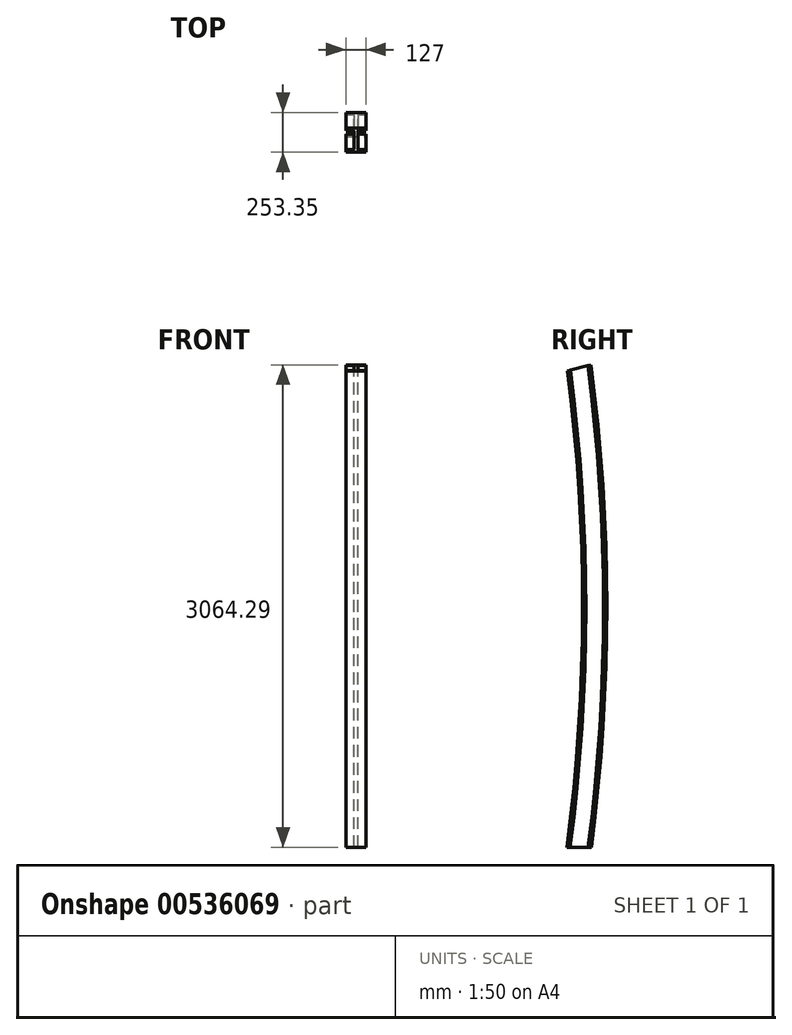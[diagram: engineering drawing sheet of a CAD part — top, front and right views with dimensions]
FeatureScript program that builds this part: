
annotation { "Feature Type Name" : "Feature", "Feature Type Description" : "" }
export const myFeature = defineFeature(function(context is Context, id is Id, definition is map)
    precondition{}
    {
        {
            var Q0;
            Q0=qCreatedBy(makeId("Top.planeOp"),FACE);
            var sketch = newSketch(context, id + "F0", { "sketchPlane" : qUnion([Q0])});
            skPoint(sketch, "E0.middle", {"position": v(0, 0) * mm});
            skLineSegment(sketch, "E1.left", {"start": v(-12.7, -57.02) * mm, "end": v(-12.7, 57.02) * mm});
            skLineSegment(sketch, "E1.right", {"start": v(12.7, -57.02) * mm, "end": v(12.7, 57.02) * mm});
            skLineSegment(sketch, "E2", {"start": v(-19.05, -63.37) * mm, "end": v(-63.5, -63.37) * mm});
            skLineSegment(sketch, "E3", {"start": v(-63.5, -63.37) * mm, "end": v(-63.5, -77.34) * mm});
            skLineSegment(sketch, "E4", {"start": v(-63.5, -77.34) * mm, "end": v(0, -77.34) * mm});
            skLineSegment(sketch, "E5.MirrorCS", {"start": v(19.05, -63.37) * mm, "end": v(63.5, -63.37) * mm});
            skLineSegment(sketch, "E6.MirrorCS", {"start": v(63.5, -63.37) * mm, "end": v(63.5, -77.34) * mm});
            skLineSegment(sketch, "E7.MirrorCS", {"start": v(63.5, -77.34) * mm, "end": v(0, -77.34) * mm});
            skLineSegment(sketch, "E8.MirrorCS", {"start": v(-19.05, 63.37) * mm, "end": v(-63.5, 63.37) * mm});
            skLineSegment(sketch, "E9.MirrorCS", {"start": v(-63.5, 77.34) * mm, "end": v(0, 77.34) * mm});
            skLineSegment(sketch, "E10.MirrorCS", {"start": v(63.5, 77.34) * mm, "end": v(0, 77.34) * mm});
            skLineSegment(sketch, "E11.MirrorCS", {"start": v(19.05, 63.37) * mm, "end": v(63.5, 63.37) * mm});
            skLineSegment(sketch, "E12.MirrorCS", {"start": v(63.5, 63.37) * mm, "end": v(63.5, 77.34) * mm});
            skLineSegment(sketch, "E13.MirrorCS", {"start": v(-63.5, 63.37) * mm, "end": v(-63.5, 77.34) * mm});
            skPoint(sketch, "E14.visualSharp", {"position": v(-12.7, -63.37) * mm});
            skArc(sketch, "E14.filletArc", {"start": v(-19.05, -63.37) * mm, "mid": v(-14.56, -61.5) * mm, "end": v(-12.7, -57.02) * mm});
            skPoint(sketch, "E15.visualSharp", {"position": v(12.7, -63.37) * mm});
            skArc(sketch, "E15.filletArc", {"start": v(12.7, -57.02) * mm, "mid": v(14.56, -61.5) * mm, "end": v(19.05, -63.37) * mm});
            skPoint(sketch, "E16.visualSharp", {"position": v(-12.7, 63.37) * mm});
            skArc(sketch, "E16.filletArc", {"start": v(-12.7, 57.02) * mm, "mid": v(-14.56, 61.5) * mm, "end": v(-19.05, 63.37) * mm});
            skPoint(sketch, "E17.visualSharp", {"position": v(12.7, 63.37) * mm});
            skArc(sketch, "E17.filletArc", {"start": v(19.05, 63.37) * mm, "mid": v(14.56, 61.5) * mm, "end": v(12.7, 57.02) * mm});
            skSolve(sketch);
        }
        {
            var Q0;
            Q0=qCreatedBy(makeId("Right.planeOp"),FACE);
            var sketch = newSketch(context, id + "F1", { "sketchPlane" : qUnion([Q0])});
            skPoint(sketch, "E18", {"position": v(0, 3044.36) * mm});
            skArc(sketch, "E19", {"start": v(0, 0) * mm, "mid": v(99.33, 1522.18) * mm, "end": v(0, 3044.36) * mm});
            skSolve(sketch);
        }
        {
            var Q0;
            Q0=makeQuery(id+"F0.imprint","IMPRINT",FACE,{"disambiguationData":[TD([[makeQuery(id+"F0.imprint","IMPRINT",EDGE,{"derivedFrom":sQuery(id+"F0.wireOp",EDGE,"E1.left")}),-1.0]])]});
            var Q1;
            Q1=sQuery(id+"F1.wireOp",EDGE,"E19");
            sweep(context, id + "F2", {"profiles" : qUnion([Q0]), "path" : qUnion([Q1])});
        }
    });
